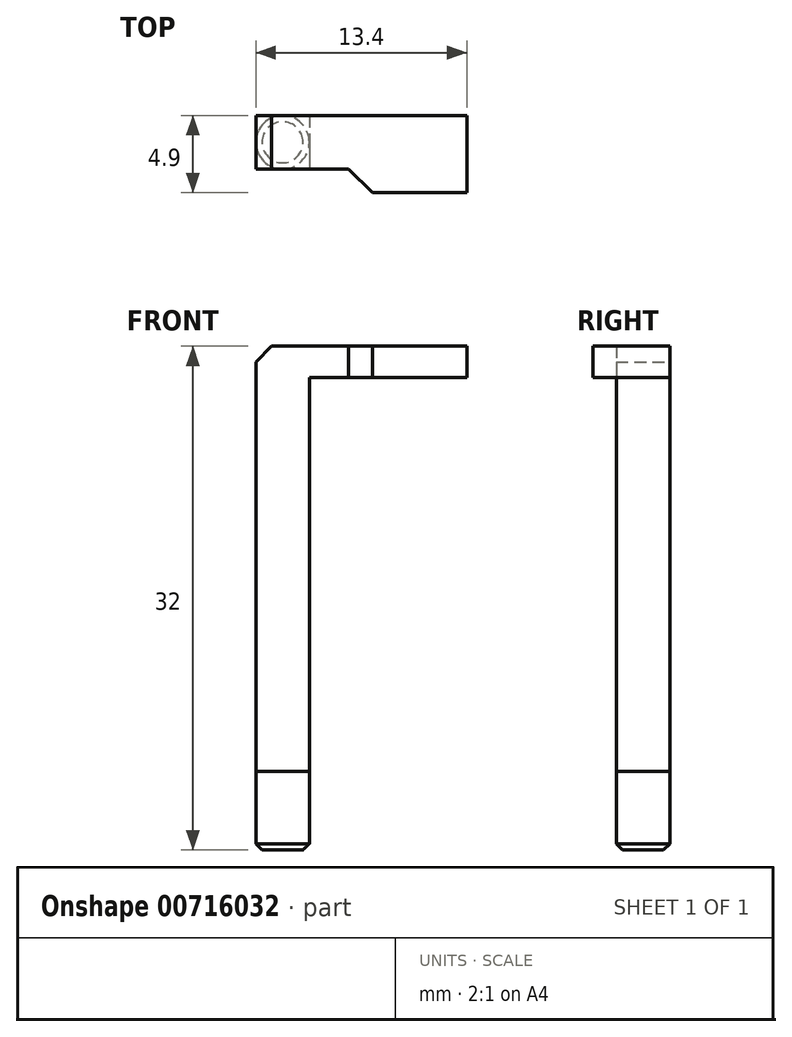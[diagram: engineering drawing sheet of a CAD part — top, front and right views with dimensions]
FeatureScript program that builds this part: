
annotation { "Feature Type Name" : "Feature", "Feature Type Description" : "" }
export const myFeature = defineFeature(function(context is Context, id is Id, definition is map)
    precondition{}
    {
        {
            var Q0;
            Q0=qCreatedBy(makeId("Top.planeOp"),FACE);
            var sketch = newSketch(context, id + "F0", { "sketchPlane" : qUnion([Q0])});
            skLineSegment(sketch, "E0.bottom", {"start": v(-1.7, 1.7) * mm, "end": v(1.7, 1.7) * mm});
            skLineSegment(sketch, "E0.top", {"start": v(-1.7, -1.7) * mm, "end": v(1.7, -1.7) * mm});
            skLineSegment(sketch, "E0.left", {"start": v(-1.7, 1.7) * mm, "end": v(-1.7, -1.7) * mm});
            skLineSegment(sketch, "E0.right", {"start": v(1.7, 1.7) * mm, "end": v(1.7, -1.7) * mm});
            skSolve(sketch);
        }
        {
            var Q0;
            Q0=qSketchRegion(id+"F0",true);
            extrude(context, id + "F1", {"entities" : qUnion([Q0]), "depth" : 27 * mm});
        }
        {
            var Q0;
            Q0=makeQuery(id+"F1.opExtrude","CAP_EDGE",EDGE,{"disambiguationData":[OSD([sQuery(id+"F0.wireOp",EDGE,"E0.left")])],"isStart":false});
            chamfer(context, id + "F2", {"entities" : qUnion([Q0]), "width" : 1 * mm, "tangentPropagation" : true});
        }
        {
            var Q0;
            Q0=makeQuery(id+"F1.opExtrude","SWEPT_FACE",FACE,{"disambiguationData":[OSD([sQuery(id+"F0.wireOp",EDGE,"E0.right")])]});
            var sketch = newSketch(context, id + "F3", { "sketchPlane" : qUnion([Q0])});
            skLineSegment(sketch, "E1.bottom", {"start": v(1.7, 27) * mm, "end": v(-3.2, 27) * mm});
            skLineSegment(sketch, "E1.top", {"start": v(1.7, 25) * mm, "end": v(-3.2, 25) * mm});
            skLineSegment(sketch, "E1.right", {"start": v(-3.2, 27) * mm, "end": v(-3.2, 25) * mm});
            skLineSegment(sketch, "E2", {"start": v(1.7, 25) * mm, "end": v(1.7, 27) * mm});
            skSolve(sketch);
        }
        {
            var Q0;
            Q0=qSketchRegion(id+"F3",true);
            extrude(context, id + "F4", {"entities" : qUnion([Q0]), "operationType" : NewBodyOperationType.ADD, "depth" : 10 * mm});
        }
        {
            var Q0;
            Q0=makeQuery(id+"F4.opExtrude","CAP_EDGE",EDGE,{"disambiguationData":[OSD([sQuery(id+"F3.wireOp",EDGE,"E1.right")])],"isStart":true});
            chamfer(context, id + "F5", {"entities" : qUnion([Q0]), "width" : 4 * mm, "tangentPropagation" : true});
        }
        {
            var Q0;
            Q0=makeQuery(id+"F0.imprint","IMPRINT",FACE,{"disambiguationData":[TD([[makeQuery(id+"F0.imprint","IMPRINT",EDGE,{"derivedFrom":sQuery(id+"F0.wireOp",EDGE,"E0.bottom")}),-1.0]])]});
            var sketch = newSketch(context, id + "F6", { "sketchPlane" : qUnion([Q0])});
            skCircle(sketch, "E3", {"center": v(0, 0) * mm, "radius": 1.7 * mm});
            skSolve(sketch);
        }
        {
            var Q0;
            {var subQ0=sQuery(id+"F6.wireOp",EDGE,"E3");var subQ1=makeQuery(id+"F6.imprint","INTERSECT",VERTEX,{"derivedFrom":[makeQuery(id+"F0.imprint","IMPRINT",EDGE,{"derivedFrom":sQuery(id+"F0.wireOp",EDGE,"E0.bottom")}),subQ0]});Q0=makeQuery(id+"F6.imprint","IMPRINT",FACE,{"disambiguationData":[TD([[makeQuery(id+"F6.imprint","IMPRINT",EDGE,{"disambiguationData":[TD([[subQ1,1.0]])],"derivedFrom":subQ0}),1.0]])]});}
            var Q1;
            Q1=sQuery(id+"F6.wireOp",EDGE,"E3");
            extrude(context, id + "F7", {"entities" : qUnion([Q0]), "operationType" : NewBodyOperationType.ADD, "surfaceEntities" : qUnion([Q1]), "oppositeDirection" : true, "depth" : 5 * mm});
        }
        {
            var Q0;
            Q0=makeQuery(id+"F7.opExtrude","CAP_EDGE",EDGE,{"disambiguationData":[OSD([sQuery(id+"F6.wireOp",EDGE,"E3")])],"isStart":false});
            chamfer(context, id + "F8", {"entities" : qUnion([Q0]), "width" : 0.4 * mm, "tangentPropagation" : true});
        }
    });
